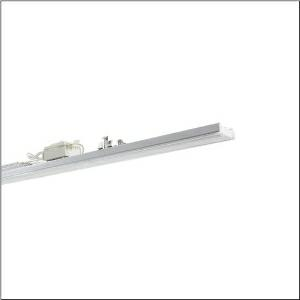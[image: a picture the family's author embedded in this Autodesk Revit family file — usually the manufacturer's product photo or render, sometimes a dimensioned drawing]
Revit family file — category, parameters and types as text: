
# Revit family: licross_r__11_recessed_mo_51tl19dv4e5g_6daf
name_source: partatom
category: Lighting Fixtures
units: mm (PartAtom-declared; Revit-internal decimal feet)

## family parameters
Cut with Voids When Loaded = No
Host = Face
Light Source = No
Part Type = Normal
Room Calculation Point = No
Round Connector Dimension = Use Diameter
Shared = No

## types (1)
- --- (1 x LED, 14720 lm, 84.1 W, 4000K)
    Apparent Load = 84 VA
    CIE Flux Codes = 55 90 98 100 100
    Color Rendering = 80
    Color Temperature = 4000K
    Default Elevation = 1800 mm
    Description = Licross® 11 Recessed MO, luminaire insert, of sheet steel, coil coated, white, length: 2.250mm, width: 66mm, height: 67mm, LED rated luminous flux: 14.720lm, light colour: 840, control gear: DALI 2, with plug, 5-pole, with phase selection, mains connection: 220..240V, AC, 50/60Hz, rated input power: 84W, internal wiring halogen-free, primary light control with lens, of plastic, primary optical cover: cover, of PMMA, light emission: direct distribution, primary light characteristic: double asymmetric, protection rating (complete): IP40, insulation class (complete): insulation class I (protective earthing), certification: CE, ENEC, VDE, UKCA, protection symbol: D if used in an environment without relevant dust loads with corresponding accessories, impact resistance: IK06, permissible ambient temperature for indoor applications: -25..+35°C, corresponds to IFS (International Featured Standards) requirements for safety and quality in the food industry, reducing of maximum allowable ambient temperature of 5°C with ceiling mounting, LABS conformity tested according to VDMA 24364:2018-05, packaging unit: 1 piece
    Height = 58 mm
    Lamp = 1 x LED
    Lamp Light Flux = 14720 lm
    Lamp Power = 84.1 W
    Lamp count = 1
    Length = 2250 mm
    Luminous efficacy = 175 lm/W
    Manufacturer = Siteco
    ModVariant = No
    Model = 51TL19DV4E5G
    Mounting Place = Ceiling
    Mounting Type = Pendant
    Number of Poles = 1
    OnlyDefault = Yes
    Power Factor = 1
    Product Name = Licross® 11 Recessed MO
    Product group = luminaire insert | ceiling pendant
    ProductGroupID = 902
    Protection Class = Protection class I
    Protection Degree = IP 40
    RLX_Detail_Level = 1
    RLX_Emergency_Light_Flux = 0 lm
    RLX_Emergency_Type = 0
    RLX_Emergency_Type_DB = No
    RlxData = <blob elided: 29477 chars, md5=19386500>
    Socket = socket
    Standby Power = 0 W
    System Light Flux = 14720 lm
    System Power = 84 W
    Type Comments = factory setting: luminous flux: 100 % | dim-lin: 254 | 378 mA
    Type Image = l_1296930.jpg
    URL = http://relux.com
    VarID = @adj_122155
    Voltage = 0 V
    Weight = 0.00 kg
    Width = 66 mm

## geometry (parser evidence)
native form markers: Blend x4, Sweep x8
no freeform markers — native parametric forms only
